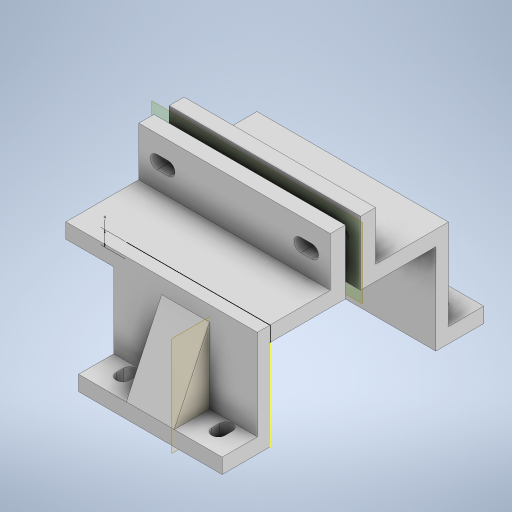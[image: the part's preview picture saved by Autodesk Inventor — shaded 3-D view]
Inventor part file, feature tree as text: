
AUTODESK INVENTOR PART (.ipt)
format: ipt  version: 2023.1 (Build 271208000, 208)  size: 797,184 bytes
history: native  units: mm
features: extrude x8, sketch x7, projected_geometry x5, other x3, plane x2, mirror x1
ambient origin geometry x8: Origin, YZ Plane, XZ Plane, XY Plane, X Axis, Y Axis, Z Axis, Center Point
bodies: Body1 (feature_tree), Body2 (feature_tree)
feature tree (26):
  other  "Left"
  extrude  "Extrusion1"  Depth=12.7mm
  extrude  "Extrusion2"  Depth=12.7mm
  plane  "Work Plane1"
  extrude  "Extrusion3"  Depth=24.0mm
  sketch  "Sketch4"  dims[d9=3.35mm d10=10.0mm d11=0.0mm]
  extrude  "Extrusion4"  Depth=10.0mm TaperAngle=0.0deg
  extrude  "Extrusion5"  Depth=25.4mm
  extrude  "Extrusion6"  Depth=3.5mm
  extrude  "Extrusion7"  Depth=3.5mm
  extrude  "Extrusion8"  [1 undecoded]
  plane  "Work Plane2"
  mirror  "Mirror1"
  sketch  "Sketch1"  dims[d0=38.1mm d1=12.7mm]
  sketch  "Sketch2"  dims[d2=12.7mm d3=12.7mm]
  projected_geometry  "Projected Loop1"
  sketch  "Sketch3"  dims[d6=4.0mm d7=0.0mm d8=24.0mm]
  projected_geometry  "Projected Loop2"
  projected_geometry  "Projected Loop3"
  sketch  "Sketch5"  dims[d12=25.4mm d13=2.0mm]
  projected_geometry  "Projected Loop4"
  sketch  "Sketch6"  dims[d14=3.5mm d15=3.5mm]
  sketch  "Sketch7"  dims[d16=3.5mm d17=3.5mm d18=-12.7mm d19=12.7mm d20=0.0mm d21=4.0mm d22=12.7mm d23=0.0mm d24=20.0mm d25=0.0mm d26=12.7mm d27=0.0mm d28=4.0mm d29=13.0mm d30=0.0mm d31=6.35mm d32=6.35mm d33=3.0mm d34=2.0mm d35=3.0mm d36=2.0mm d37=3.5mm d38=3.5mm d39=13.0mm d40=0.0mm d41=2.0mm]
  projected_geometry  "Projected Loop5"
  other  "Pattern of Left:1"
  other  "Right"
note: 1 required parameter value undecoded (feature->parameter linkage not recoverable at this tier; creation-order binding heuristic only, values carry confidence <= 0.55)
